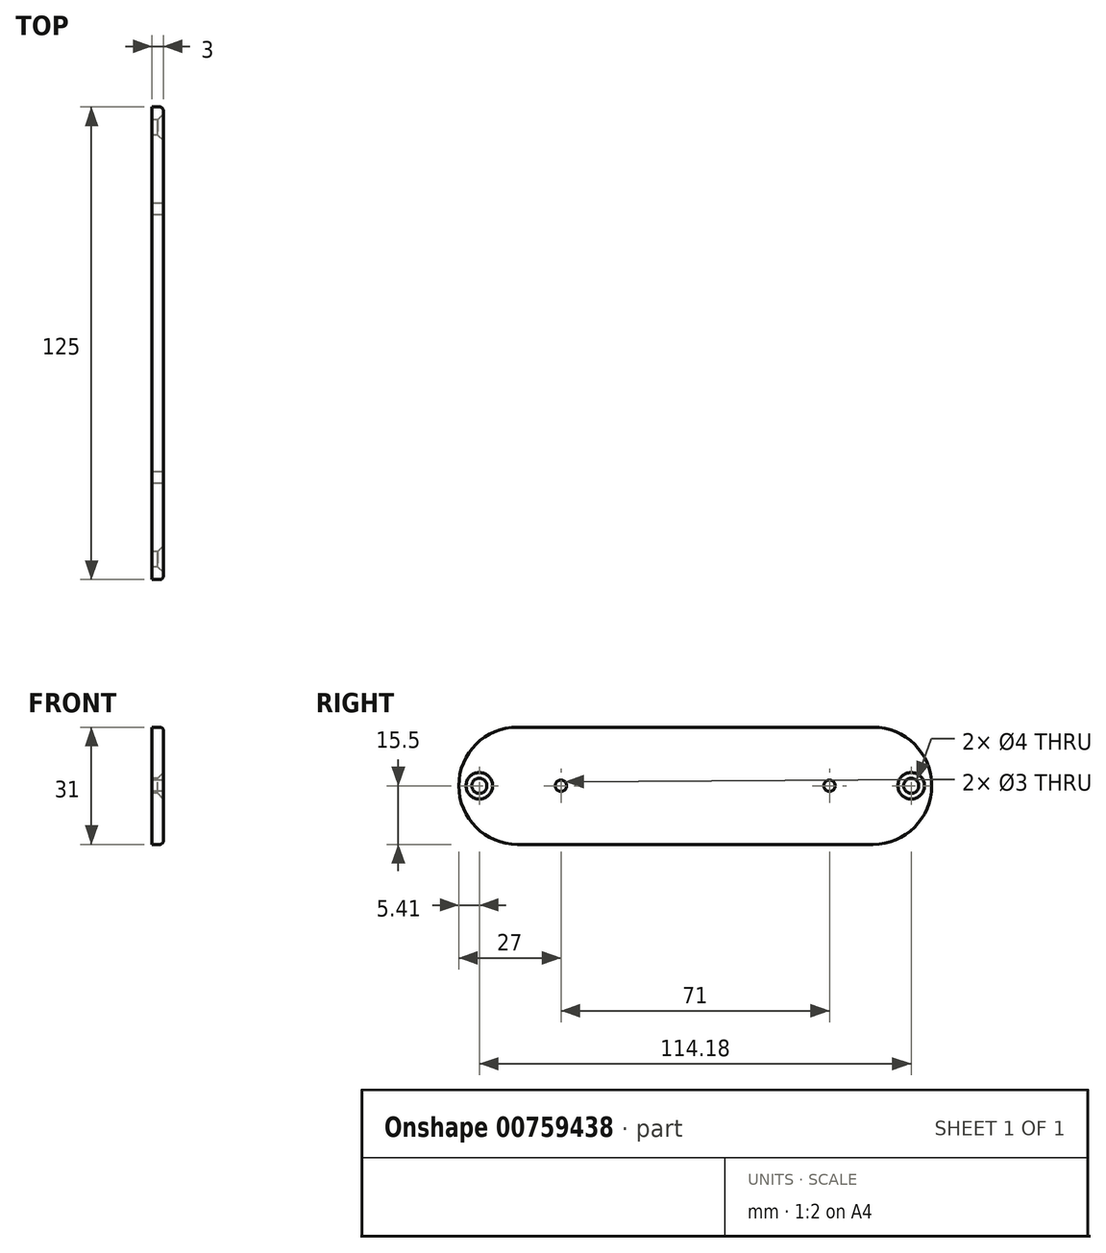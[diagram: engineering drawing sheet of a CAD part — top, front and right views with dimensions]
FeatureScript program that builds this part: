
annotation { "Feature Type Name" : "Feature", "Feature Type Description" : "" }
export const myFeature = defineFeature(function(context is Context, id is Id, definition is map)
    precondition{}
    {
        {
            var Q0;
            Q0=qCreatedBy(makeId("Right.planeOp"),FACE);
            var sketch = newSketch(context, id + "F0", { "sketchPlane" : qUnion([Q0])});
            skLineSegment(sketch, "E0", {"start": v(0, 15.5) * mm, "end": v(-47, 15.5) * mm});
            skArc(sketch, "E1", {"start": v(-47, 15.5) * mm, "mid": v(-62.5, 0) * mm, "end": v(-47, -15.5) * mm});
            skLineSegment(sketch, "E2.MirrorCS", {"start": v(0, -15.5) * mm, "end": v(-47, -15.5) * mm});
            skLineSegment(sketch, "E3.MirrorCS", {"start": v(0, 15.5) * mm, "end": v(47, 15.5) * mm});
            skArc(sketch, "E4.MirrorCS", {"start": v(47, 15.5) * mm, "mid": v(62.5, 0) * mm, "end": v(47, -15.5) * mm});
            skLineSegment(sketch, "E5.MirrorCS", {"start": v(0, -15.5) * mm, "end": v(47, -15.5) * mm});
            skCircle(sketch, "E6", {"center": v(57.1, 0) * mm, "radius": 2 * mm});
            skCircle(sketch, "E7", {"center": v(35.5, 0) * mm, "radius": 1.5 * mm});
            skCircle(sketch, "E8.MirrorC", {"center": v(-35.5, 0) * mm, "radius": 1.5 * mm});
            skCircle(sketch, "E9.MirrorC", {"center": v(-57.1, 0) * mm, "radius": 2 * mm});
            skSolve(sketch);
        }
        {
            var Q0;
            Q0 = qSketchRegion(id + "F0", true);
            extrude(context, id + "F1", {"entities" : qUnion([Q0]), "endBound" : BoundingType.SYMMETRIC, "depth" : 3 * mm, "offsetDistance" : 25 * mm});
        }
        {
            var Q0;
            Q0=makeQuery(id+"F1.opExtrude","CAP_EDGE",EDGE,{"disambiguationData":[OSD([sQuery(id+"F0.wireOp",EDGE,"E9.MirrorC")])],"isStart":false});
            var Q1;
            Q1=makeQuery(id+"F1.opExtrude","CAP_EDGE",EDGE,{"disambiguationData":[OSD([sQuery(id+"F0.wireOp",EDGE,"E6")])],"isStart":false});
            chamfer(context, id + "F2", {"entities" : qUnion([Q0, Q1]), "width" : 1.5 * mm, "tangentPropagation" : true});
        }
        {
            var Q0;
            Q0=makeQuery(id+"F1.opExtrude","CAP_EDGE",EDGE,{"disambiguationData":[OSD([sQuery(id+"F0.wireOp",EDGE,"E2.MirrorCS"),sQuery(id+"F0.wireOp",EDGE,"E5.MirrorCS")])],"isStart":false});
            fillet(context, id + "F3", {"entities" : qUnion([Q0]), "radius" : 1 * mm, "tangentPropagation" : true, "allowEdgeOverflow" : false});
        }
    });
